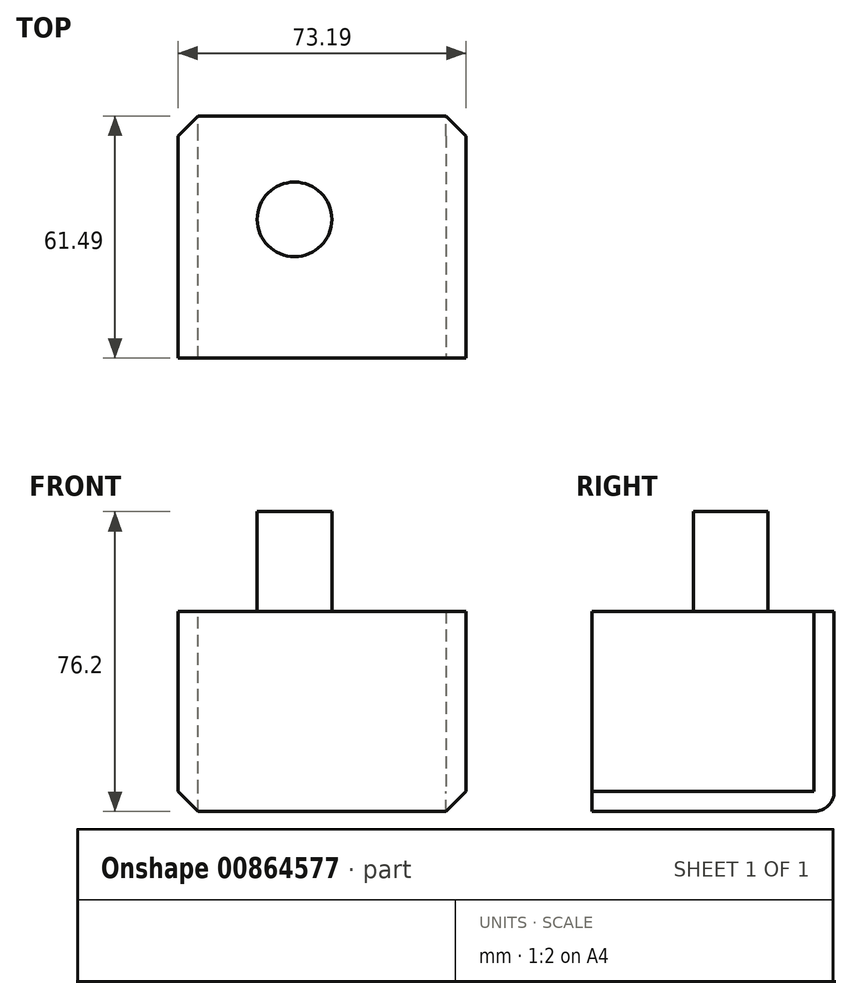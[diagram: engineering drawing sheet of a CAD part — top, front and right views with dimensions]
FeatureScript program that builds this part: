
annotation { "Feature Type Name" : "Feature", "Feature Type Description" : "" }
export const myFeature = defineFeature(function(context is Context, id is Id, definition is map)
    precondition{}
    {
        {
            var Q0;
            Q0=qCreatedBy(makeId("Top.planeOp"),FACE);
            var sketch = newSketch(context, id + "F0", { "sketchPlane" : qUnion([Q0])});
            skLineSegment(sketch, "E0.bottom", {"start": v(-31.18, 27.28) * mm, "end": v(42, 27.28) * mm});
            skLineSegment(sketch, "E0.top", {"start": v(-31.18, -34.21) * mm, "end": v(42, -34.21) * mm});
            skLineSegment(sketch, "E0.left", {"start": v(-31.18, 27.28) * mm, "end": v(-31.18, -34.21) * mm});
            skLineSegment(sketch, "E0.right", {"start": v(42, 27.28) * mm, "end": v(42, -34.21) * mm});
            skLineSegment(sketch, "E1.bottom", {"start": v(5.41, 27.28) * mm, "end": v(5.41, 27.28) * mm});
            skLineSegment(sketch, "E1.top", {"start": v(5.41, -34.21) * mm, "end": v(5.41, -34.21) * mm});
            skLineSegment(sketch, "E1.left", {"start": v(5.41, 27.28) * mm, "end": v(5.41, -34.21) * mm});
            skLineSegment(sketch, "E1.right", {"start": v(5.41, 27.28) * mm, "end": v(5.41, -34.21) * mm});
            skSolve(sketch);
        }
        {
            var Q0;
            Q0 = qSketchRegion(id + "F0", true);
            extrude(context, id + "F1", {"entities" : qUnion([Q0]), "depth" : 25.4 * mm, "offsetDistance" : 25.4 * mm});
        }
        {
            var Q0;
            Q0=makeQuery(id+"F1.opExtrude","CAP_FACE",FACE,{"disambiguationData":[OSD([sQuery(id+"F0.wireOp",EDGE,"E0.bottom"),sQuery(id+"F0.wireOp",EDGE,"E0.top"),sQuery(id+"F0.wireOp",EDGE,"E0.left"),sQuery(id+"F0.wireOp",EDGE,"E0.right")])],"isStart":false});
            extrude(context, id + "F2", {"entities" : qUnion([Q0]), "operationType" : NewBodyOperationType.ADD, "depth" : 25.4 * mm, "offsetDistance" : 25.4 * mm});
        }
        {
            var Q0;
            Q0=makeQuery(id+"F1.opExtrude","CAP_EDGE",EDGE,{"disambiguationData":[OSD([sQuery(id+"F0.wireOp",EDGE,"E0.bottom")])],"isStart":true});
            fillet(context, id + "F3", {"entities" : qUnion([Q0]), "radius" : 5.08 * mm, "tangentPropagation" : true, "allowEdgeOverflow" : false});
        }
        {
            var Q0;
            {var subQ0=sQuery(id+"F0.wireOp",EDGE,"E0.left");var subQ1=sQuery(id+"F0.wireOp",EDGE,"E0.bottom");Q0=makeQuery(id+"F2.boolean.opBoolean","MERGE",EDGE,{"derivedFrom":[makeQuery(id+"F1.opExtrude","SWEPT_EDGE",EDGE,{"disambiguationData":[OSD([subQ1,subQ0])]}),makeQuery(id+"F2.opExtrude","SWEPT_EDGE",EDGE,{"disambiguationData":[OSD([subQ1,subQ0])]})]});}
            var Q1;
            {var subQ0=sQuery(id+"F0.wireOp",EDGE,"E0.right");var subQ1=sQuery(id+"F0.wireOp",EDGE,"E0.bottom");Q1=makeQuery(id+"F2.boolean.opBoolean","MERGE",EDGE,{"derivedFrom":[makeQuery(id+"F1.opExtrude","SWEPT_EDGE",EDGE,{"disambiguationData":[OSD([subQ1,subQ0])]}),makeQuery(id+"F2.opExtrude","SWEPT_EDGE",EDGE,{"disambiguationData":[OSD([subQ1,subQ0])]})]});}
            var Q2;
            Q2=makeQuery(id+"F1.opExtrude","CAP_EDGE",EDGE,{"disambiguationData":[OSD([sQuery(id+"F0.wireOp",EDGE,"E0.right")])],"isStart":true});
            chamfer(context, id + "F4", {"entities" : qUnion([Q0, Q1, Q2]), "width" : 5.08 * mm, "tangentPropagation" : true});
        }
        {
            var Q0;
            Q0=makeQuery(id+"F2.opExtrude","CAP_FACE",FACE,{"disambiguationData":[OSD([sQuery(id+"F0.wireOp",EDGE,"E0.bottom"),sQuery(id+"F0.wireOp",EDGE,"E0.top"),sQuery(id+"F0.wireOp",EDGE,"E0.left"),sQuery(id+"F0.wireOp",EDGE,"E0.right")])],"isStart":false});
            var sketch = newSketch(context, id + "F5", { "sketchPlane" : qUnion([Q0])});
            skCircle(sketch, "E2", {"center": v(-1.6, 1.02) * mm, "radius": 9.48 * mm});
            skPoint(sketch, "E2.first.point", {"position": v(0, 10.37) * mm});
            skPoint(sketch, "E2.second.point", {"position": v(7.83, 0) * mm});
            skPoint(sketch, "E2.third.point", {"position": v(-11.01, 0) * mm});
            skSolve(sketch);
        }
        {
            var Q0;
            Q0 = qSketchRegion(id + "F5", true);
            extrude(context, id + "F6", {"entities" : qUnion([Q0]), "operationType" : NewBodyOperationType.ADD, "depth" : 25.4 * mm, "offsetDistance" : 25.4 * mm});
        }
    });
